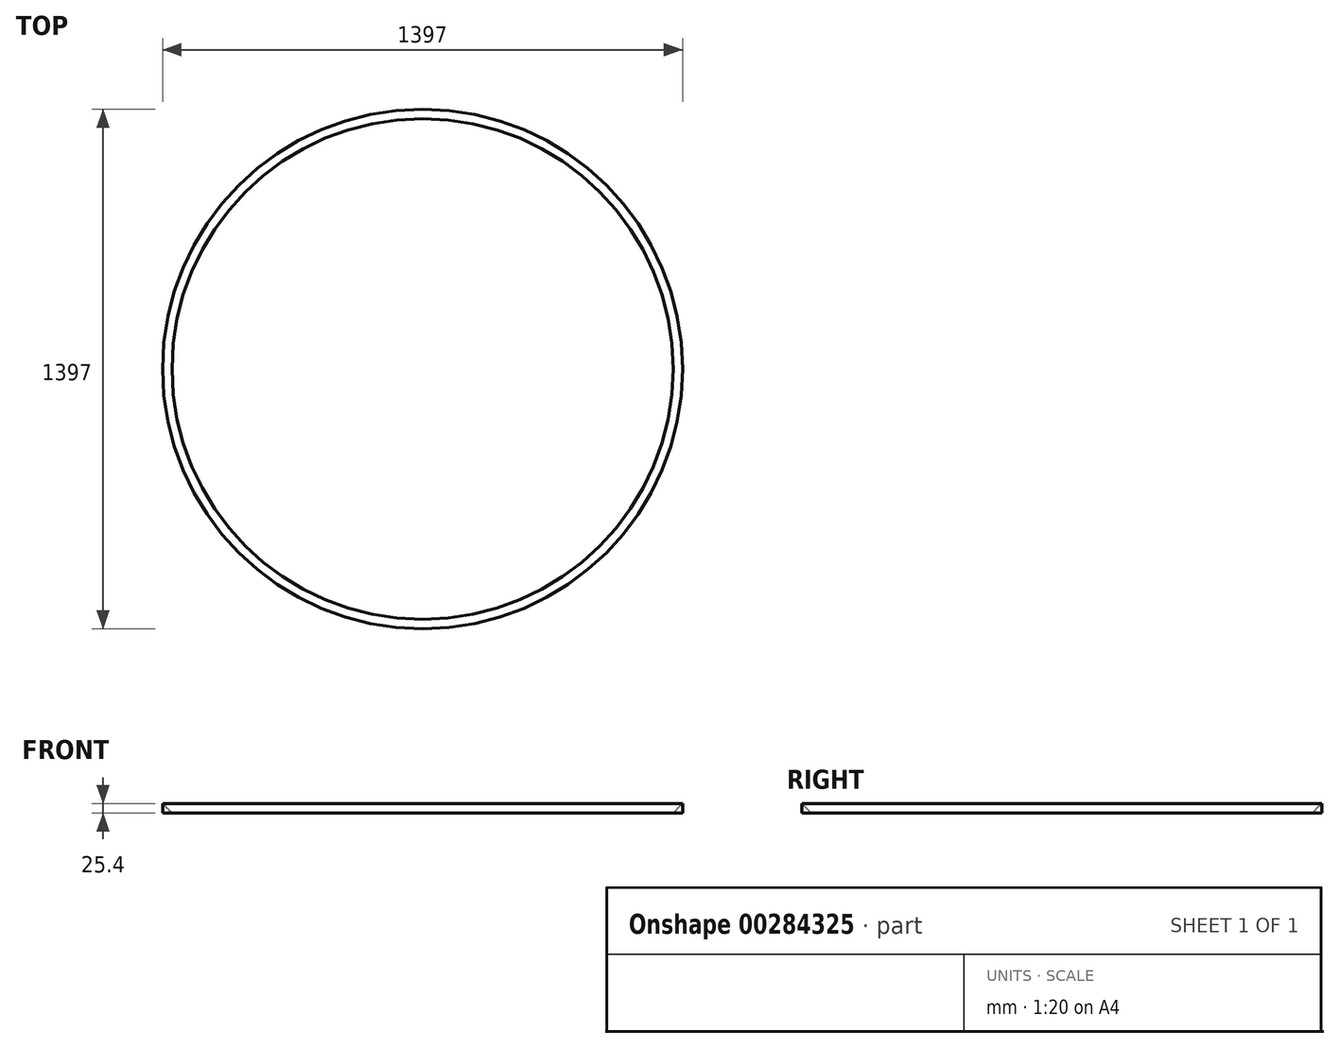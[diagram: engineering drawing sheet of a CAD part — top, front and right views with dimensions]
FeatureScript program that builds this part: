
annotation { "Feature Type Name" : "Feature", "Feature Type Description" : "" }
export const myFeature = defineFeature(function(context is Context, id is Id, definition is map)
    precondition{}
    {
        {
            var Q0;
            Q0=qCreatedBy(makeId("Top.planeOp"),FACE);
            var sketch = newSketch(context, id + "F0", { "sketchPlane" : qUnion([Q0])});
            skCircle(sketch, "E0", {"center": v(0, 0) * mm, "radius": 673.1 * mm});
            skSolve(sketch);
        }
        {
            var Q0;
            Q0=qCreatedBy(makeId("Front.planeOp"),FACE);
            var sketch = newSketch(context, id + "F1", { "sketchPlane" : qUnion([Q0])});
            skLineSegment(sketch, "E1.0", {"start": v(-673.1, 0) * mm, "end": v(673.1, 0) * mm, "construction": true});
            skLineSegment(sketch, "E2", {"start": v(-673.1, 0) * mm, "end": v(-698.5, 25.4) * mm});
            skLineSegment(sketch, "E3", {"start": v(-698.5, 25.4) * mm, "end": v(-698.5, 0) * mm});
            skLineSegment(sketch, "E4", {"start": v(-698.5, 0) * mm, "end": v(-673.1, 0) * mm});
            skSolve(sketch);
        }
        {
            var Q0;
            Q0=makeQuery(id+"F1.imprint","IMPRINT",FACE,{"disambiguationData":[TD([[makeQuery(id+"F1.imprint","IMPRINT",EDGE,{"derivedFrom":sQuery(id+"F1.wireOp",EDGE,"E2")}),1.0]])]});
            var Q1;
            Q1=sQuery(id+"F0.wireOp",EDGE,"E0");
            revolve(context, id + "F2", {"surfaceOperationType" : NewSurfaceOperationType.NEW, "entities" : qUnion([Q0]), "axis" : qUnion([Q1]), "revolveType" : RevolveType.FULL});
        }
    });
